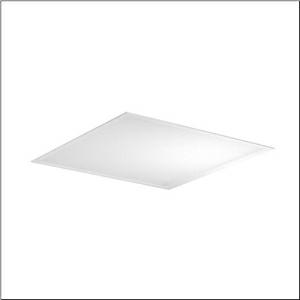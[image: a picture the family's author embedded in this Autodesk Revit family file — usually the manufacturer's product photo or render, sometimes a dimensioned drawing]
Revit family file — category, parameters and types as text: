
# Revit family: apollon_r__21_square_51mq12wd2t13_0a2d
name_source: partatom
category: Lighting Fixtures
units: mm (PartAtom-declared; Revit-internal decimal feet)

## family parameters
Cut with Voids When Loaded = No
Host = Face
Light Source = No
Part Type = Normal
Room Calculation Point = No
Round Connector Dimension = Use Diameter
Shared = No

## types (1)
- --- (1 x LED 2700 K ... 6500 K, 4000 lm, 40 W, 2700K)
    Apparent Load = 40 VA
    CIE Flux Codes = 61 87 97 100 100
    Color Rendering = 80
    Color Temperature = 2700K
    Default Elevation = 1800 mm
    Description = Apollon® 21 square, office luminaire, primary optical cover: micro prismatic cover, of PMMA, CAT 2 (L<= 3000cd/m²), light emission: direct distribution, primary light characteristic: symmetric, installation type: lay-in mounting, LED, rated luminous flux: 4.000lm, luminous efficacy: 100lm/W, light colour: 8tw, colour temperature: 2700..6500K, control gear: DALI-2 DT8, with terminal, 5-pole, mains connection: 220..240V, AC, 50/60Hz, rated input power: 40W, housing, of aluminium, traffic white (RAL 9016), module: M600, length: 596mm, width: 596mm, height: 40mm, housing upper side, of sheet steel, galvanised, protection rating (complete): IP20, protection rating (lamp compartment, on room side): IP50, insulation class (complete): insulation class I (protective earthing), certification: CE, ENEC, permissible operating ambient temperature: -20..+40°C, packaging unit: 1 piece
    Height = 0 mm  [stored 0 ft]
    Lamp = 1 x LED 2700 K ... 6500 K
    Lamp Light Flux = 4000 lm
    Lamp Power = 40 W
    Lamp count = 1
    Length = 595 mm
    Luminous efficacy = 100 lm/W
    Manufacturer = Siteco
    ModVariant = No
    Model = 51MQ12WD2T13
    Mounting Place = Ceiling
    Mounting Type = Recessed
    Number of Poles = 1
    OnlyDefault = Yes
    Power Factor = 1
    Product Name = Apollon® 21 square
    Product group = office luminaire | ceiling recessed
    ProductGroupID = 401
    Protection Class = Protection class I
    Protection Degree = IP 20
    RLX_Detail_Level = 1
    RLX_Emergency_Light_Flux = 0 lm
    RLX_Emergency_Type = 0
    RLX_Emergency_Type_DB = No
    RlxData = <blob elided: 12661 chars, md5=fd9e9291>
    Socket = socket
    Standby Power = 0 W
    System Light Flux = 4000 lm
    System Power = 40 W
    Type Comments = individual setting: CCT=2700K
    Type Image = l_1291049.jpg
    URL = http://relux.com
    VarID = @adj_102358
    Voltage = 0 V
    Weight = 0.00 kg
    Width = 595 mm

note: [stored X ft] marks values corroborated as IEEE doubles in the binary element streams (Revit-internal decimal feet)

## geometry (parser evidence)
native form markers: Sweep x10
no freeform markers — native parametric forms only
